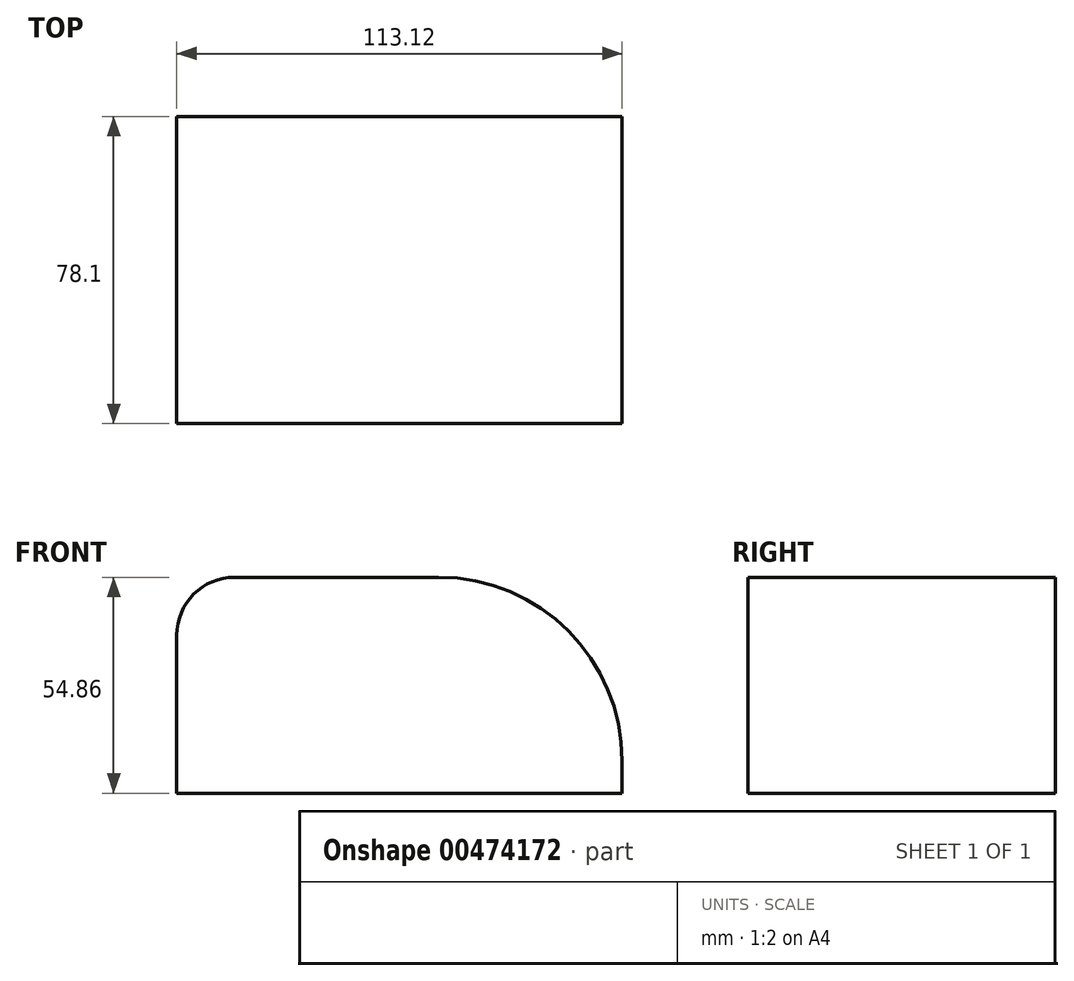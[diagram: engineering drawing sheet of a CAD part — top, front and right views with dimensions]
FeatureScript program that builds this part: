
annotation { "Feature Type Name" : "Feature", "Feature Type Description" : "" }
export const myFeature = defineFeature(function(context is Context, id is Id, definition is map)
    precondition{}
    {
        {
            var Q0;
            Q0=qCreatedBy(makeId("Top.planeOp"),FACE);
            var sketch = newSketch(context, id + "F0", { "sketchPlane" : qUnion([Q0])});
            skLineSegment(sketch, "E0.bottom", {"start": v(-54.35, 35.53) * mm, "end": v(58.77, 35.53) * mm});
            skLineSegment(sketch, "E0.top", {"start": v(-54.35, -42.57) * mm, "end": v(58.77, -42.57) * mm});
            skLineSegment(sketch, "E0.left", {"start": v(-54.35, 35.53) * mm, "end": v(-54.35, -42.57) * mm});
            skLineSegment(sketch, "E0.right", {"start": v(58.77, 35.53) * mm, "end": v(58.77, -42.57) * mm});
            skSolve(sketch);
        }
        {
            var Q0;
            Q0=makeQuery(id+"F0.imprint","IMPRINT",FACE,{"disambiguationData":[TD([[makeQuery(id+"F0.imprint","IMPRINT",EDGE,{"derivedFrom":sQuery(id+"F0.wireOp",EDGE,"E0.bottom")}),-1.0]])]});
            extrude(context, id + "F1", {"entities" : qUnion([Q0]), "depth" : 54.86 * mm});
        }
        {
            var Q0;
            Q0=makeQuery(id+"F1.opExtrude","CAP_EDGE",EDGE,{"disambiguationData":[OSD([sQuery(id+"F0.wireOp",EDGE,"E0.right")])],"isStart":false});
            fillet(context, id + "F2", {"entities" : qUnion([Q0]), "radius" : 46.6 * mm, "tangentPropagation" : true, "allowEdgeOverflow" : false});
        }
        {
            var Q0;
            Q0=makeQuery(id+"F1.opExtrude","CAP_EDGE",EDGE,{"disambiguationData":[OSD([sQuery(id+"F0.wireOp",EDGE,"E0.left")])],"isStart":false});
            fillet(context, id + "F3", {"entities" : qUnion([Q0]), "radius" : 14.72 * mm, "tangentPropagation" : true, "allowEdgeOverflow" : false});
        }
    });
